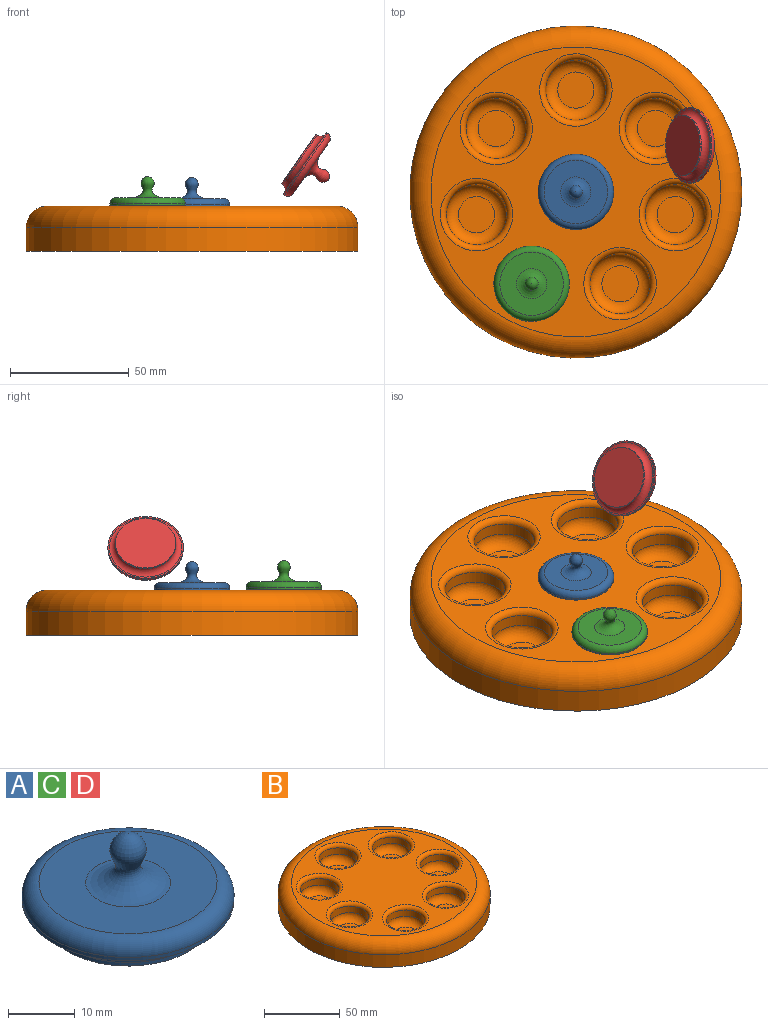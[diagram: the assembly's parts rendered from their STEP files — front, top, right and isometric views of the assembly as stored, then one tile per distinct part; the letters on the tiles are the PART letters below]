
ASSEMBLY  parts=4 mates=2
PART A: 8 faces, bbox 36.9x36.9x16.4 mm
  f0: cylinder r=12.7mm len=25.4mm, axis (0,0,-1), area 50.7mm2, adj f1,f6
  f1: plane 25.4x25.4mm, normal (0,0,-1), area 506.7mm2, adj f0
  f2: cylinder r=15.88mm len=31.75mm, axis (0,0,-1), area 63.3mm2, adj f4,f5
  f3: plane 26.67x26.67mm, normal (0,0,1), area 432mm2, adj f5,f7
  f4: plane 31.75x31.75mm, normal (0,0,-1), area 62.1mm2, adj f2,f6
  f5: torus R=13.33mm, axis (0,0,1), area 374.8mm2, adj f2,f3
  f6: torus R=15.24mm, axis (0,0,1), area 341.5mm2, adj f0,f4
  f7: revolved ~12.7x12.7mm, area 229.7mm2, adj f3
PART B: 32 faces, bbox 151.2x151.2x19.1 mm
  f0: cylinder r=69.85mm len=139.7mm, axis (0,0,-1), area 4459mm2, adj f2,f3
  f1: plane 121.92x121.92mm, normal (0,0,1), area 6566.9mm2, adj f3,f25,f26,f27,f28,f29,f30,f31
  f2: plane 139.7x139.7mm, normal (0,0,-1), area 15327.9mm2, adj f0
  f3: torus R=60.96mm, axis (0,0,1), area 5845.3mm2, adj f0,f1
  f4: cylinder r=12.7mm len=25.4mm, axis (0,0,1), area 405.4mm2, adj f24,f31
  f5: plane 15.24x15.24mm, normal (0,0,1), area 182.4mm2, adj f24
  f6: cylinder r=12.7mm len=25.4mm, axis (0,0,1), area 405.4mm2, adj f18,f25
  f7: plane 15.24x15.24mm, normal (0,0,1), area 182.4mm2, adj f18
  f8: cylinder r=12.7mm len=25.4mm, axis (0,0,1), area 405.4mm2, adj f19,f26
  f9: plane 15.24x15.24mm, normal (0,0,1), area 182.4mm2, adj f19
  f10: cylinder r=12.7mm len=25.4mm, axis (0,0,1), area 405.4mm2, adj f20,f27
  f11: plane 15.24x15.24mm, normal (0,0,1), area 182.4mm2, adj f20
  f12: cylinder r=12.7mm len=25.4mm, axis (0,0,1), area 405.4mm2, adj f21,f28
  f13: plane 15.24x15.24mm, normal (0,0,1), area 182.4mm2, adj f21
  f14: cylinder r=12.7mm len=25.4mm, axis (0,0,1), area 405.4mm2, adj f22,f29
  f15: plane 15.24x15.24mm, normal (0,0,1), area 182.4mm2, adj f22
  f16: cylinder r=12.7mm len=25.4mm, axis (0,0,1), area 405.4mm2, adj f23,f30
  f17: plane 15.24x15.24mm, normal (0,0,1), area 182.4mm2, adj f23
  f18: torus R=7.62mm, axis (0,0,1), area 544.2mm2, adj f6,f7
  f19: torus R=7.62mm, axis (0,0,1), area 544.2mm2, adj f8,f9
  f20: torus R=7.62mm, axis (0,0,1), area 544.2mm2, adj f10,f11
  f21: torus R=7.62mm, axis (0,0,1), area 544.2mm2, adj f12,f13
  f22: torus R=7.62mm, axis (0,0,1), area 544.2mm2, adj f14,f15
  f23: torus R=7.62mm, axis (0,0,1), area 544.2mm2, adj f16,f17
  f24: torus R=7.62mm, axis (0,0,1), area 544.2mm2, adj f4,f5
  f25: torus R=15.24mm, axis (0,0,1), area 341.5mm2, adj f1,f6
  f26: torus R=15.24mm, axis (0,0,1), area 341.5mm2, adj f1,f8
  f27: torus R=15.24mm, axis (0,0,1), area 341.5mm2, adj f1,f10
  f28: torus R=15.24mm, axis (0,0,1), area 341.5mm2, adj f1,f12
  f29: torus R=15.24mm, axis (0,0,1), area 341.5mm2, adj f1,f14
  f30: torus R=15.24mm, axis (0,0,1), area 341.5mm2, adj f1,f16
  f31: torus R=15.24mm, axis (0,0,1), area 341.5mm2, adj f1,f4
PART C: same geometry as A
PART D: same geometry as A
PLACE A t=(-23.84,12.61,41.21)mm
PLACE B t=(-23.84,12.61,25.33)mm
PLACE C t=(-42.43,-26.01,41.63)mm
PLACE D rot(axis=(0,1,0),125deg) t=(21.13,32.12,64.18)mm
MATE cylindrical B.f10 <-> C.f0  axis (0,0,1) through (-42.43,-26.01,43.64)mm
MATE fastened A.f2 <-> B.f0  axis (0,0,-1) through (-23.84,12.61,44.38)mm
